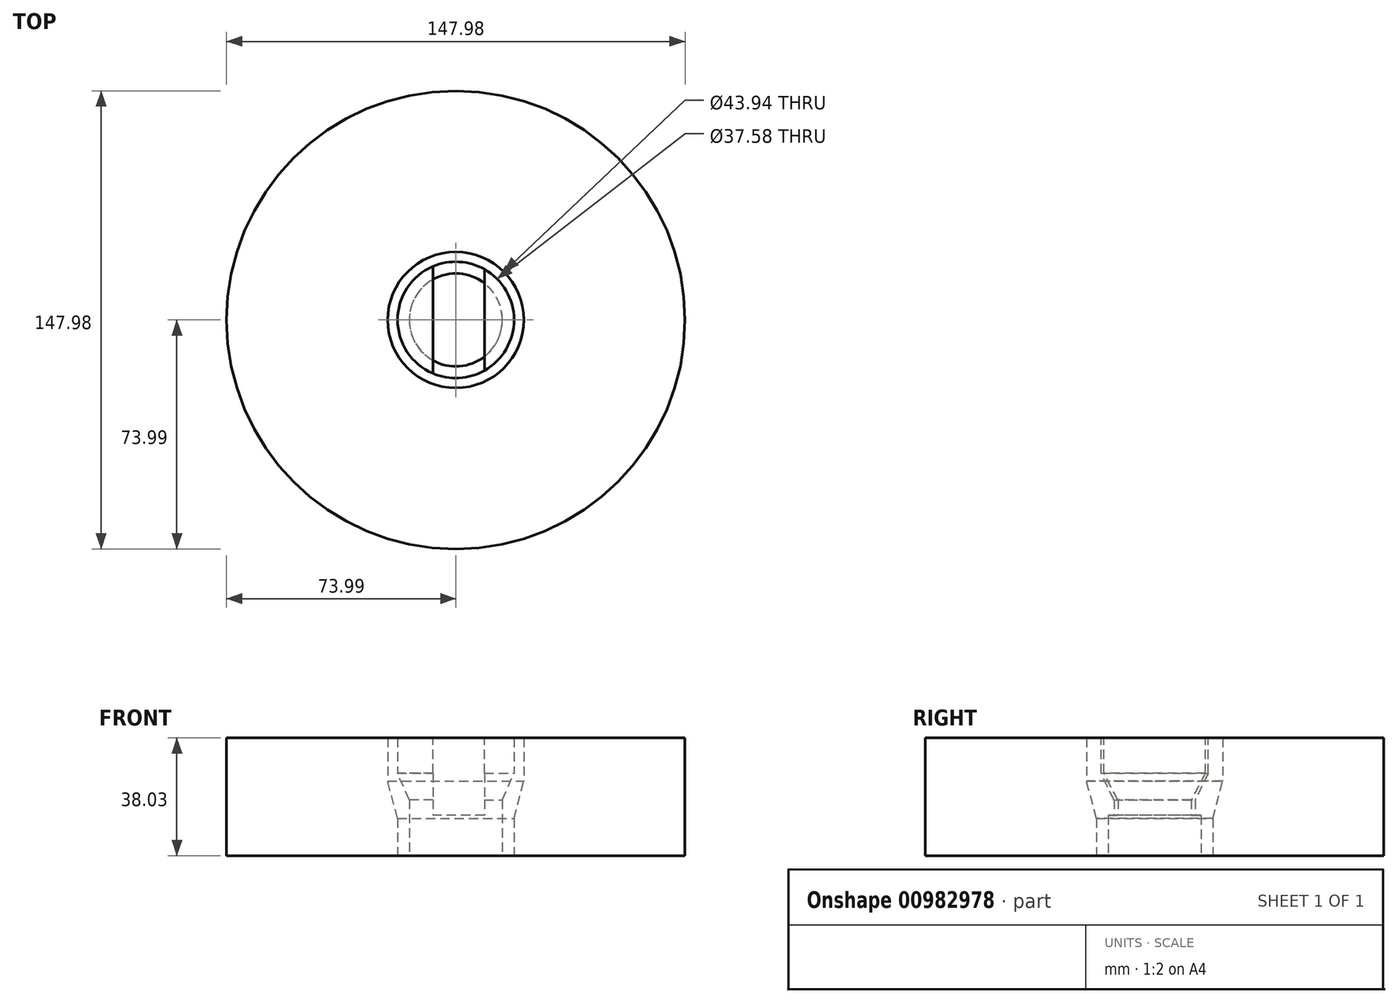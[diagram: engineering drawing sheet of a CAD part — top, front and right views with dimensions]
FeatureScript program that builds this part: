
annotation { "Feature Type Name" : "Feature", "Feature Type Description" : "" }
export const myFeature = defineFeature(function(context is Context, id is Id, definition is map)
    precondition{}
    {
        {
            var Q0;
            Q0=qCreatedBy(makeId("Front.planeOp"),FACE);
            var sketch = newSketch(context, id + "F0", { "sketchPlane" : qUnion([Q0])});
            skLineSegment(sketch, "E0", {"start": v(0, 0) * mm, "end": v(0, 38.03) * mm});
            skLineSegment(sketch, "E1", {"start": v(0, 38.03) * mm, "end": v(18.8, 38.03) * mm});
            skLineSegment(sketch, "E2", {"start": v(18.8, 38.03) * mm, "end": v(18.8, 26.61) * mm});
            skLineSegment(sketch, "E3", {"start": v(18.8, 26.61) * mm, "end": v(15.02, 18.04) * mm});
            skLineSegment(sketch, "E4", {"start": v(15.02, 18.04) * mm, "end": v(15.02, 0) * mm});
            skLineSegment(sketch, "E5", {"start": v(15.02, 0) * mm, "end": v(0, 0) * mm});
            skLineSegment(sketch, "E6", {"start": v(21.97, 38.03) * mm, "end": v(21.97, 24.02) * mm});
            skLineSegment(sketch, "E7", {"start": v(21.97, 24.02) * mm, "end": v(18.8, 12) * mm});
            skLineSegment(sketch, "E8", {"start": v(18.8, 12) * mm, "end": v(18.8, 0) * mm});
            skLineSegment(sketch, "E9", {"start": v(18.8, 0) * mm, "end": v(73.99, 0) * mm});
            skLineSegment(sketch, "E10", {"start": v(73.99, 0) * mm, "end": v(73.99, 38.03) * mm});
            skLineSegment(sketch, "E11", {"start": v(73.99, 38.03) * mm, "end": v(21.97, 38.03) * mm});
            skSolve(sketch);
        }
        {
            var Q0;
            Q0=makeQuery(id+"F0.imprint","IMPRINT",FACE,{"disambiguationData":[TD([[makeQuery(id+"F0.imprint","IMPRINT",EDGE,{"derivedFrom":sQuery(id+"F0.wireOp",EDGE,"E0")}),-1.0]])]});
            var Q1;
            Q1=makeQuery(id+"F0.imprint","IMPRINT",FACE,{"disambiguationData":[TD([[makeQuery(id+"F0.imprint","IMPRINT",EDGE,{"derivedFrom":sQuery(id+"F0.wireOp",EDGE,"E6")}),1.0]])]});
            var Q2;
            Q2=sQuery(id+"F0.wireOp",EDGE,"E0");
            revolve(context, id + "F1", {"surfaceOperationType" : NewSurfaceOperationType.NEW, "entities" : qUnion([Q0, Q1]), "axis" : qUnion([Q2]), "revolveType" : RevolveType.FULL});
        }
        {
            var Q0;
            Q0=makeQuery(id+"F1.opRevolve","SWEPT_FACE",FACE,{"disambiguationData":[OSD([sQuery(id+"F0.wireOp",EDGE,"E1")])]});
            var sketch = newSketch(context, id + "F2", { "sketchPlane" : qUnion([Q0])});
            skLineSegment(sketch, "E12", {"start": v(-7.35, 17.3) * mm, "end": v(-7.35, -17.3) * mm});
            skLineSegment(sketch, "E13", {"start": v(9.26, 16.35) * mm, "end": v(9.26, -16.35) * mm});
            skSolve(sketch);
        }
        {
            var Q0;
            {var subQ0=sQuery(id+"F2.wireOp",EDGE,"E12");Q0=makeQuery(id+"F2.imprint","IMPRINT",FACE,{"disambiguationData":[TD([[makeQuery(id+"F2.imprint","IMPRINT",EDGE,{"derivedFrom":subQ0}),1.0]])]});}
            extrude(context, id + "F3", {"entities" : qUnion([Q0]), "operationType" : NewBodyOperationType.REMOVE, "oppositeDirection" : true, "depth" : 25 * mm, "offsetDistance" : 25 * mm});
        }
    });
